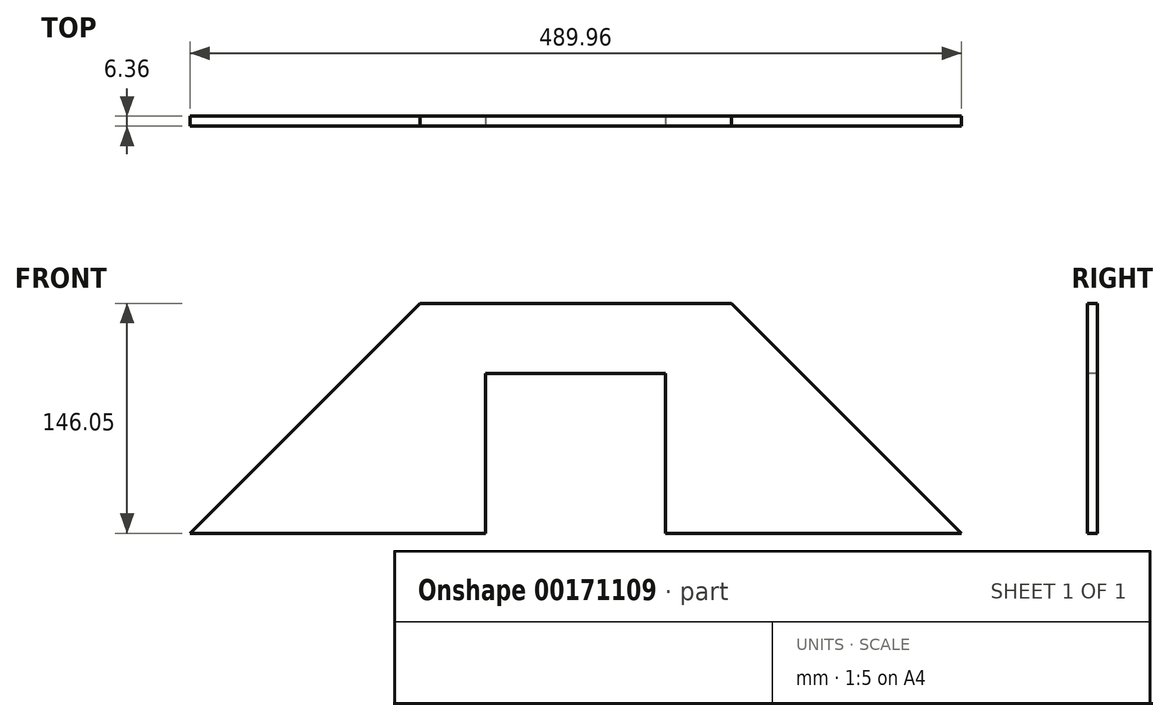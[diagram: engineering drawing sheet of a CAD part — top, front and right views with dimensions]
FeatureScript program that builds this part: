
annotation { "Feature Type Name" : "Feature", "Feature Type Description" : "" }
export const myFeature = defineFeature(function(context is Context, id is Id, definition is map)
    precondition{}
    {
        {
            var Q0;
            Q0=qCreatedBy(makeId("Front.planeOp"),FACE);
            var sketch = newSketch(context, id + "F0", { "sketchPlane" : qUnion([Q0])});
            skLineSegment(sketch, "E0", {"start": v(-98.93, 0) * mm, "end": v(98.93, 0) * mm});
            skLineSegment(sketch, "E1", {"start": v(98.93, 0) * mm, "end": v(244.98, -146.05) * mm});
            skLineSegment(sketch, "E2", {"start": v(244.98, -146.05) * mm, "end": v(-244.98, -146.05) * mm});
            skLineSegment(sketch, "E3", {"start": v(-244.98, -146.05) * mm, "end": v(-98.93, 0) * mm});
            skSolve(sketch);
        }
        {
            var Q0;
            Q0 = qSketchRegion(id + "F0", true);
            extrude(context, id + "F1", {"entities" : qUnion([Q0]), "endBound" : BoundingType.SYMMETRIC, "depth" : 6.35 * mm});
        }
        {
            var Q0;
            Q0=makeQuery(id+"F1.opExtrude","CAP_FACE",FACE,{"disambiguationData":[OSD([sQuery(id+"F0.wireOp",EDGE,"E0"),sQuery(id+"F0.wireOp",EDGE,"E1"),sQuery(id+"F0.wireOp",EDGE,"E2"),sQuery(id+"F0.wireOp",EDGE,"E3")])],"isStart":false});
            var sketch = newSketch(context, id + "F2", { "sketchPlane" : qUnion([Q0])});
            skLineSegment(sketch, "E4", {"start": v(0, 0) * mm, "end": v(0, -146.05) * mm});
            skLineSegment(sketch, "E5.bottom", {"start": v(-57.15, -44.45) * mm, "end": v(57.15, -44.45) * mm});
            skLineSegment(sketch, "E5.top", {"start": v(-57.15, -146.05) * mm, "end": v(57.15, -146.05) * mm});
            skLineSegment(sketch, "E5.left", {"start": v(-57.15, -44.45) * mm, "end": v(-57.15, -146.05) * mm});
            skLineSegment(sketch, "E5.right", {"start": v(57.15, -44.45) * mm, "end": v(57.15, -146.05) * mm});
            skPoint(sketch, "E6", {"position": v(0, -44.45) * mm});
            skSolve(sketch);
        }
        {
            var Q0;
            Q0 = qSketchRegion(id + "F2", true);
            extrude(context, id + "F3", {"entities" : qUnion([Q0]), "operationType" : NewBodyOperationType.REMOVE, "endBound" : BoundingType.THROUGH_ALL, "oppositeDirection" : true, "depth" : 25.4 * mm});
        }
    });
